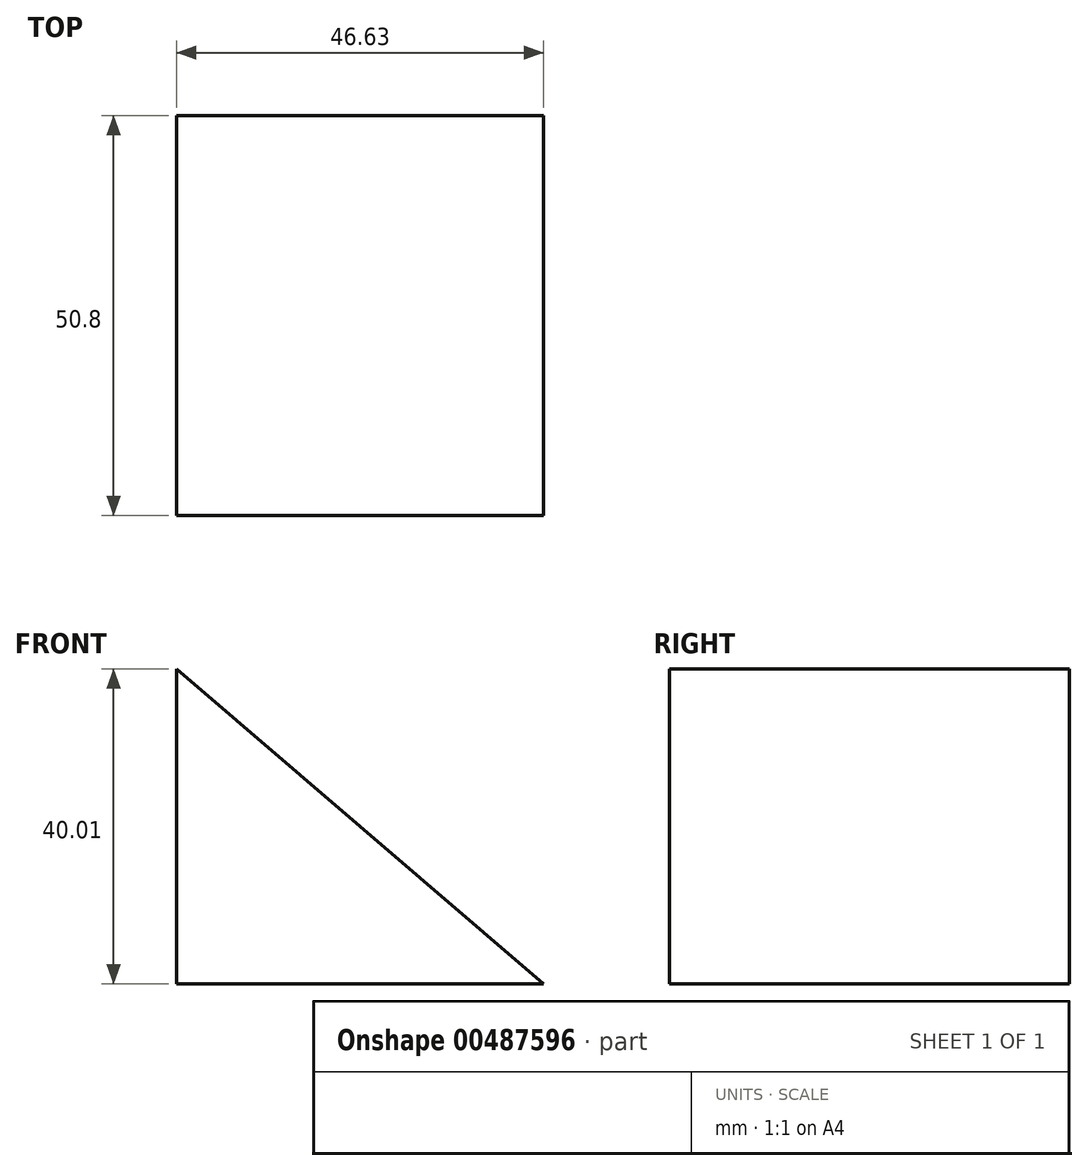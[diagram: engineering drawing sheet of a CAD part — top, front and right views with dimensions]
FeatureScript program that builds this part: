
annotation { "Feature Type Name" : "Feature", "Feature Type Description" : "" }
export const myFeature = defineFeature(function(context is Context, id is Id, definition is map)
    precondition{}
    {
        {
            var Q0;
            Q0=qCreatedBy(makeId("Front.planeOp"),FACE);
            var sketch = newSketch(context, id + "F0", { "sketchPlane" : qUnion([Q0])});
            skLineSegment(sketch, "E0", {"start": v(-30.8, 40) * mm, "end": v(-30.8, 0) * mm});
            skLineSegment(sketch, "E1", {"start": v(-30.8, 0) * mm, "end": v(15.83, 0) * mm});
            skLineSegment(sketch, "E2", {"start": v(15.83, 0) * mm, "end": v(-30.8, 40) * mm});
            skSolve(sketch);
        }
        {
            var Q0;
            Q0=makeQuery(id+"F0.imprint","IMPRINT",FACE,{"disambiguationData":[TD([[makeQuery(id+"F0.imprint","IMPRINT",EDGE,{"derivedFrom":sQuery(id+"F0.wireOp",EDGE,"E0")}),1.0]])]});
            extrude(context, id + "F1", {"entities" : qUnion([Q0]), "depth" : 25.4 * mm});
        }
        {
            var Q0;
            Q0=makeQuery(id+"F1.opExtrude","CAP_FACE",FACE,{"disambiguationData":[OSD([sQuery(id+"F0.wireOp",EDGE,"E0"),sQuery(id+"F0.wireOp",EDGE,"E1"),sQuery(id+"F0.wireOp",EDGE,"E2")])],"isStart":true});
            var sketch = newSketch(context, id + "F2", { "sketchPlane" : qUnion([Q0])});
            skLineSegment(sketch, "E3", {"start": v(30.8, 40) * mm, "end": v(30.8, 0) * mm});
            skLineSegment(sketch, "E4", {"start": v(30.8, 40) * mm, "end": v(-15.83, 0) * mm});
            skSolve(sketch);
        }
        {
            var Q0;
            Q0=makeQuery(id+"F2.imprint","IMPRINT",FACE,{"disambiguationData":[TD([[makeQuery(id+"F2.imprint","IMPRINT",EDGE,{"derivedFrom":sQuery(id+"F2.wireOp",EDGE,"E3")}),-1.0]])]});
            extrude(context, id + "F3", {"entities" : qUnion([Q0]), "operationType" : NewBodyOperationType.ADD, "depth" : 25.4 * mm});
        }
    });
